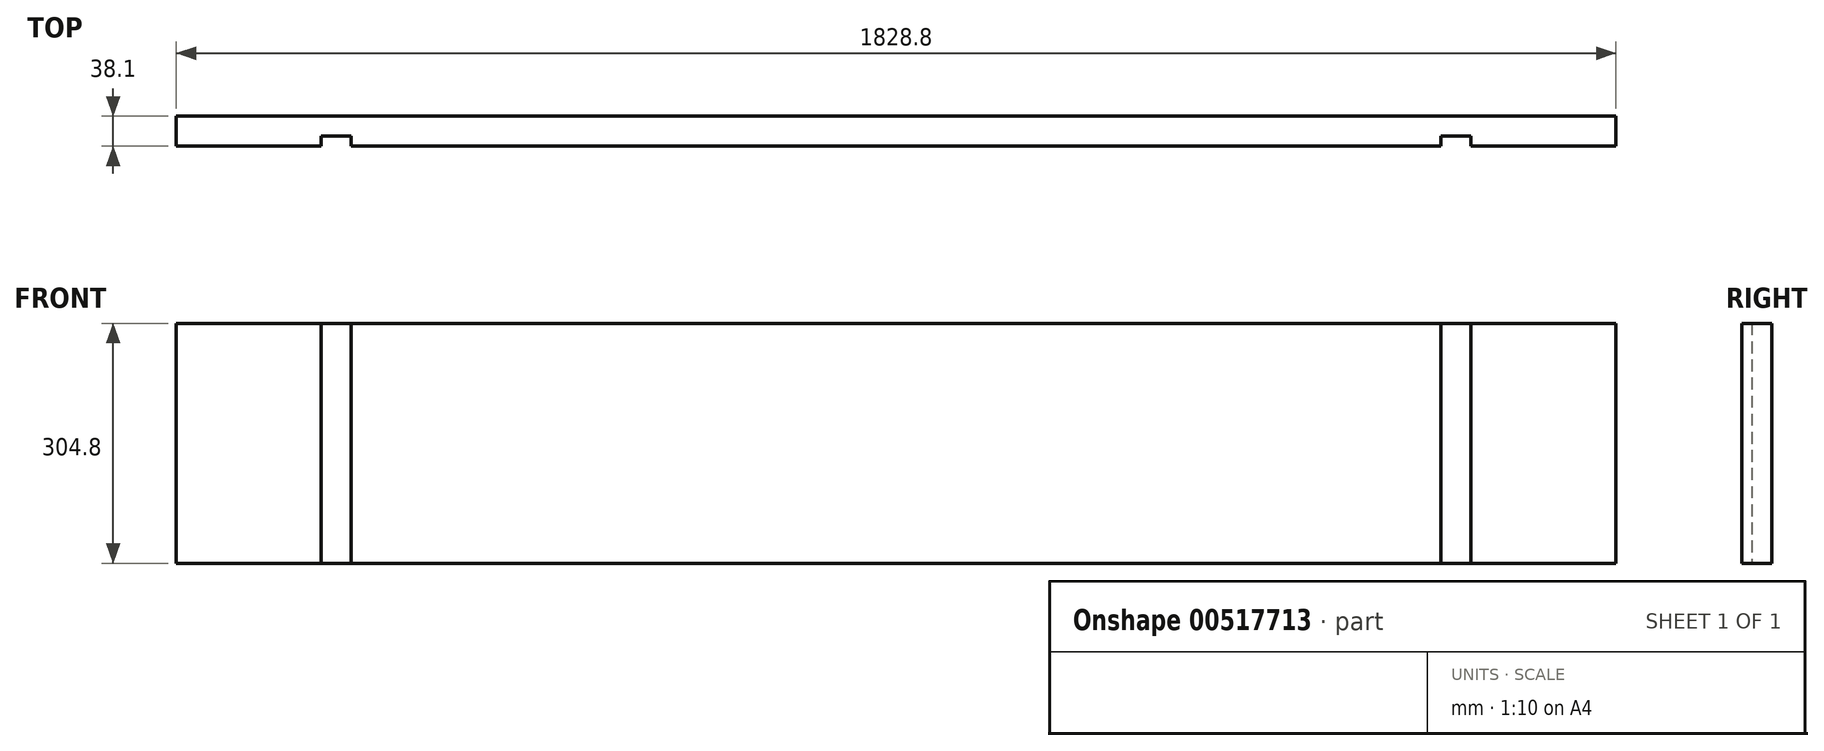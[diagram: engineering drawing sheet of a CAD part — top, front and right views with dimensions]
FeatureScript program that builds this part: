
annotation { "Feature Type Name" : "Feature", "Feature Type Description" : "" }
export const myFeature = defineFeature(function(context is Context, id is Id, definition is map)
    precondition{}
    {
        {
            var Q0;
            Q0=qCreatedBy(makeId("Front.planeOp"),FACE);
            var sketch = newSketch(context, id + "F0", { "sketchPlane" : qUnion([Q0])});
            skLineSegment(sketch, "E0.bottom", {"start": v(914.4, 152.4) * mm, "end": v(-914.4, 152.4) * mm});
            skLineSegment(sketch, "E0.top", {"start": v(914.4, -152.4) * mm, "end": v(-914.4, -152.4) * mm});
            skLineSegment(sketch, "E0.left", {"start": v(914.4, 152.4) * mm, "end": v(914.4, -152.4) * mm});
            skLineSegment(sketch, "E0.right", {"start": v(-914.4, 152.4) * mm, "end": v(-914.4, -152.4) * mm});
            skPoint(sketch, "E0.middle", {"position": v(0, 0) * mm});
            skSolve(sketch);
        }
        {
            var Q0;
            Q0 = qSketchRegion(id + "F0", true);
            extrude(context, id + "F1", {"entities" : qUnion([Q0]), "depth" : 38.1 * mm, "offsetDistance" : 25.4 * mm});
        }
        {
            var Q0;
            Q0=makeQuery(id+"F1.opExtrude","CAP_FACE",FACE,{"disambiguationData":[OSD([sQuery(id+"F0.wireOp",EDGE,"E0.bottom"),sQuery(id+"F0.wireOp",EDGE,"E0.top"),sQuery(id+"F0.wireOp",EDGE,"E0.left"),sQuery(id+"F0.wireOp",EDGE,"E0.right")])],"isStart":false});
            var sketch = newSketch(context, id + "F2", { "sketchPlane" : qUnion([Q0])});
            skLineSegment(sketch, "E1.bottom", {"start": v(730.25, 152.4) * mm, "end": v(692.15, 152.4) * mm});
            skLineSegment(sketch, "E1.top", {"start": v(730.25, -152.4) * mm, "end": v(692.15, -152.4) * mm});
            skLineSegment(sketch, "E1.left", {"start": v(730.25, 152.4) * mm, "end": v(730.25, -152.4) * mm});
            skLineSegment(sketch, "E1.right", {"start": v(692.15, 152.4) * mm, "end": v(692.15, -152.4) * mm});
            skLineSegment(sketch, "E2.bottom", {"start": v(-730.25, 152.4) * mm, "end": v(-692.15, 152.4) * mm});
            skLineSegment(sketch, "E2.top", {"start": v(-730.25, -152.4) * mm, "end": v(-692.15, -152.4) * mm});
            skLineSegment(sketch, "E2.left", {"start": v(-730.25, 152.4) * mm, "end": v(-730.25, -152.4) * mm});
            skLineSegment(sketch, "E2.right", {"start": v(-692.15, 152.4) * mm, "end": v(-692.15, -152.4) * mm});
            skSolve(sketch);
        }
        {
            var Q0;
            Q0=makeQuery(id+"F2.imprint","IMPRINT",FACE,{"disambiguationData":[TD([[makeQuery(id+"F2.imprint","IMPRINT",EDGE,{"derivedFrom":sQuery(id+"F2.wireOp",EDGE,"E1.bottom")}),1.0]])]});
            var Q1;
            Q1=makeQuery(id+"F2.imprint","IMPRINT",FACE,{"disambiguationData":[TD([[makeQuery(id+"F2.imprint","IMPRINT",EDGE,{"derivedFrom":sQuery(id+"F2.wireOp",EDGE,"E2.bottom")}),1.0]])]});
            extrude(context, id + "F3", {"entities" : qUnion([Q0, Q1]), "operationType" : NewBodyOperationType.REMOVE, "oppositeDirection" : true, "depth" : 12.7 * mm, "offsetDistance" : 25.4 * mm});
        }
    });
